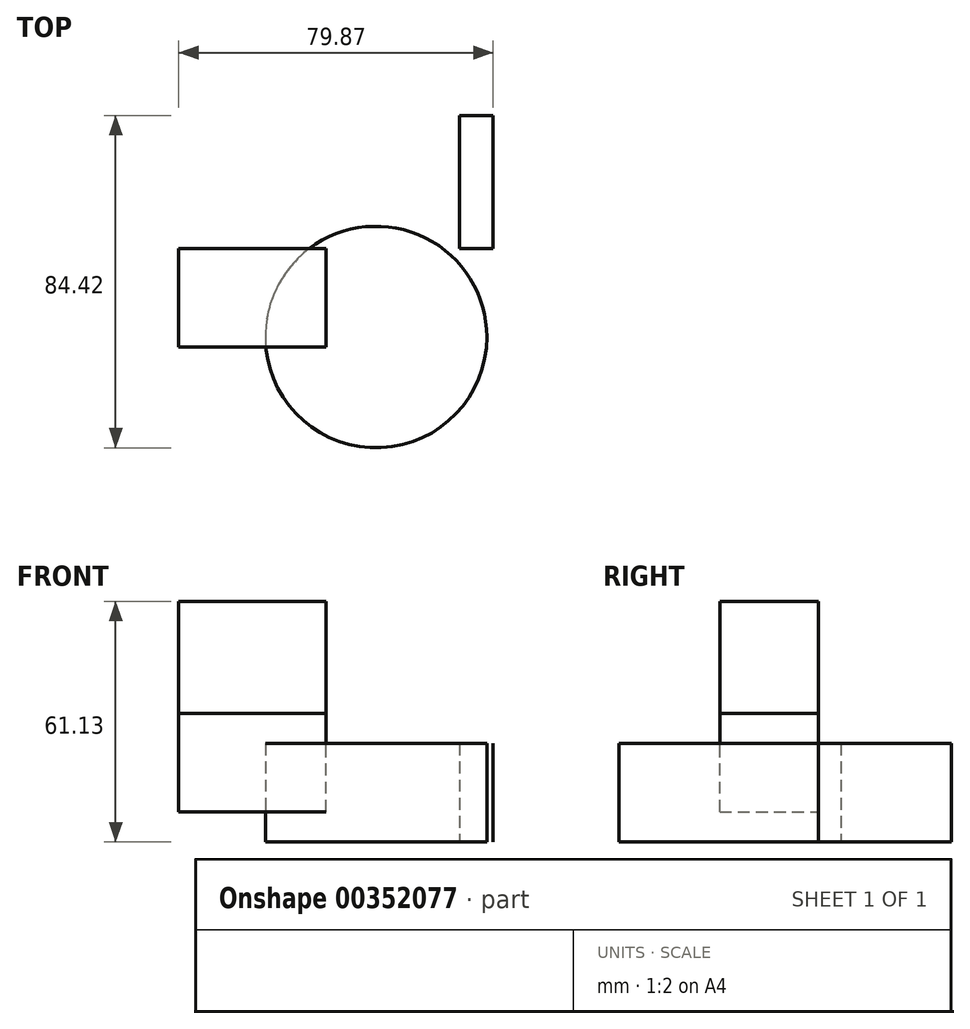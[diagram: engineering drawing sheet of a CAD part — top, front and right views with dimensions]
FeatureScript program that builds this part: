
annotation { "Feature Type Name" : "Feature", "Feature Type Description" : "" }
export const myFeature = defineFeature(function(context is Context, id is Id, definition is map)
    precondition{}
    {
        {
            var Q0;
            Q0=qCreatedBy(makeId("Top.planeOp"),FACE);
            var sketch = newSketch(context, id + "F0", { "sketchPlane" : qUnion([Q0])});
            skLineSegment(sketch, "E0.bottom", {"start": v(0, 0) * mm, "end": v(8.55, 0) * mm});
            skLineSegment(sketch, "E0.top", {"start": v(0, 33.85) * mm, "end": v(8.55, 33.85) * mm});
            skLineSegment(sketch, "E0.left", {"start": v(0, 0) * mm, "end": v(0, 33.85) * mm});
            skLineSegment(sketch, "E0.right", {"start": v(8.55, 0) * mm, "end": v(8.55, 33.85) * mm});
            skSolve(sketch);
        }
        {
            var Q0;
            Q0 = qSketchRegion(id + "F0", true);
            extrude(context, id + "F1", {"entities" : qUnion([Q0]), "depth" : 25 * mm});
        }
        {
            var Q0;
            Q0=qCreatedBy(makeId("Front.planeOp"),FACE);
            var sketch = newSketch(context, id + "F2", { "sketchPlane" : qUnion([Q0])});
            skLineSegment(sketch, "E1.bottom", {"start": v(-71.32, 32.7) * mm, "end": v(-33.87, 32.7) * mm});
            skLineSegment(sketch, "E1.top", {"start": v(-71.32, 61.13) * mm, "end": v(-33.87, 61.13) * mm});
            skLineSegment(sketch, "E1.left", {"start": v(-71.32, 32.7) * mm, "end": v(-71.32, 61.13) * mm});
            skLineSegment(sketch, "E1.right", {"start": v(-33.87, 32.7) * mm, "end": v(-33.87, 61.13) * mm});
            skSolve(sketch);
        }
        {
            var Q0;
            Q0 = qSketchRegion(id + "F2", true);
            extrude(context, id + "F3", {"entities" : qUnion([Q0]), "depth" : 25 * mm});
        }
        {
            var Q0;
            Q0=qCreatedBy(makeId("Top.planeOp"),FACE);
            var sketch = newSketch(context, id + "F4", { "sketchPlane" : qUnion([Q0])});
            skCircle(sketch, "E2", {"center": v(-21.2, -22.43) * mm, "radius": 28.14 * mm});
            skSolve(sketch);
        }
        {
            var Q0;
            Q0 = qSketchRegion(id + "F4", true);
            extrude(context, id + "F5", {"entities" : qUnion([Q0]), "depth" : 25 * mm});
        }
        {
            var Q0;
            Q0=makeQuery(id+"F3.opExtrude","SWEPT_FACE",FACE,{"disambiguationData":[OSD([sQuery(id+"F2.wireOp",EDGE,"E1.bottom")])]});
            extrude(context, id + "F6", {"entities" : qUnion([Q0]), "depth" : 25 * mm});
        }
    });
